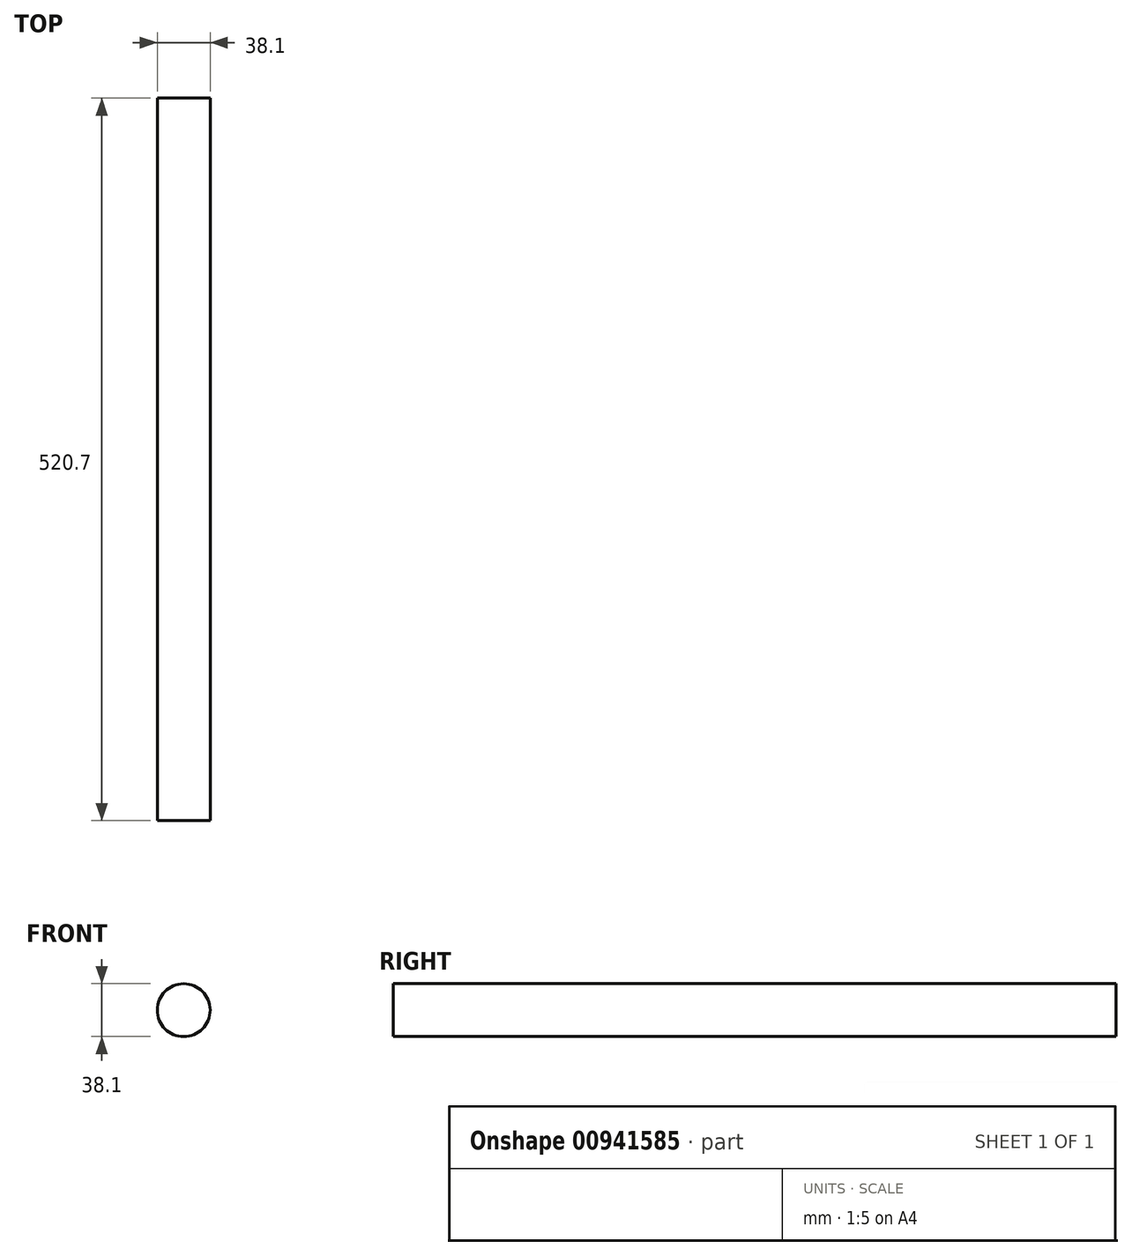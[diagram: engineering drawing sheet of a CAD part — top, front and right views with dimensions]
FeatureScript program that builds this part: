
annotation { "Feature Type Name" : "Feature", "Feature Type Description" : "" }
export const myFeature = defineFeature(function(context is Context, id is Id, definition is map)
    precondition{}
    {
        {
            var Q0;
            Q0=qCreatedBy(makeId("Front.planeOp"),FACE);
            var sketch = newSketch(context, id + "F0", { "sketchPlane" : qUnion([Q0])});
            skCircle(sketch, "E0", {"center": v(0, 0) * mm, "radius": 19.05 * mm});
            skSolve(sketch);
        }
        {
            var Q0;
            Q0 = qSketchRegion(id + "F0", true);
            extrude(context, id + "F1", {"entities" : qUnion([Q0]), "depth" : 520.7 * mm, "offsetDistance" : 25.4 * mm});
        }
    });
